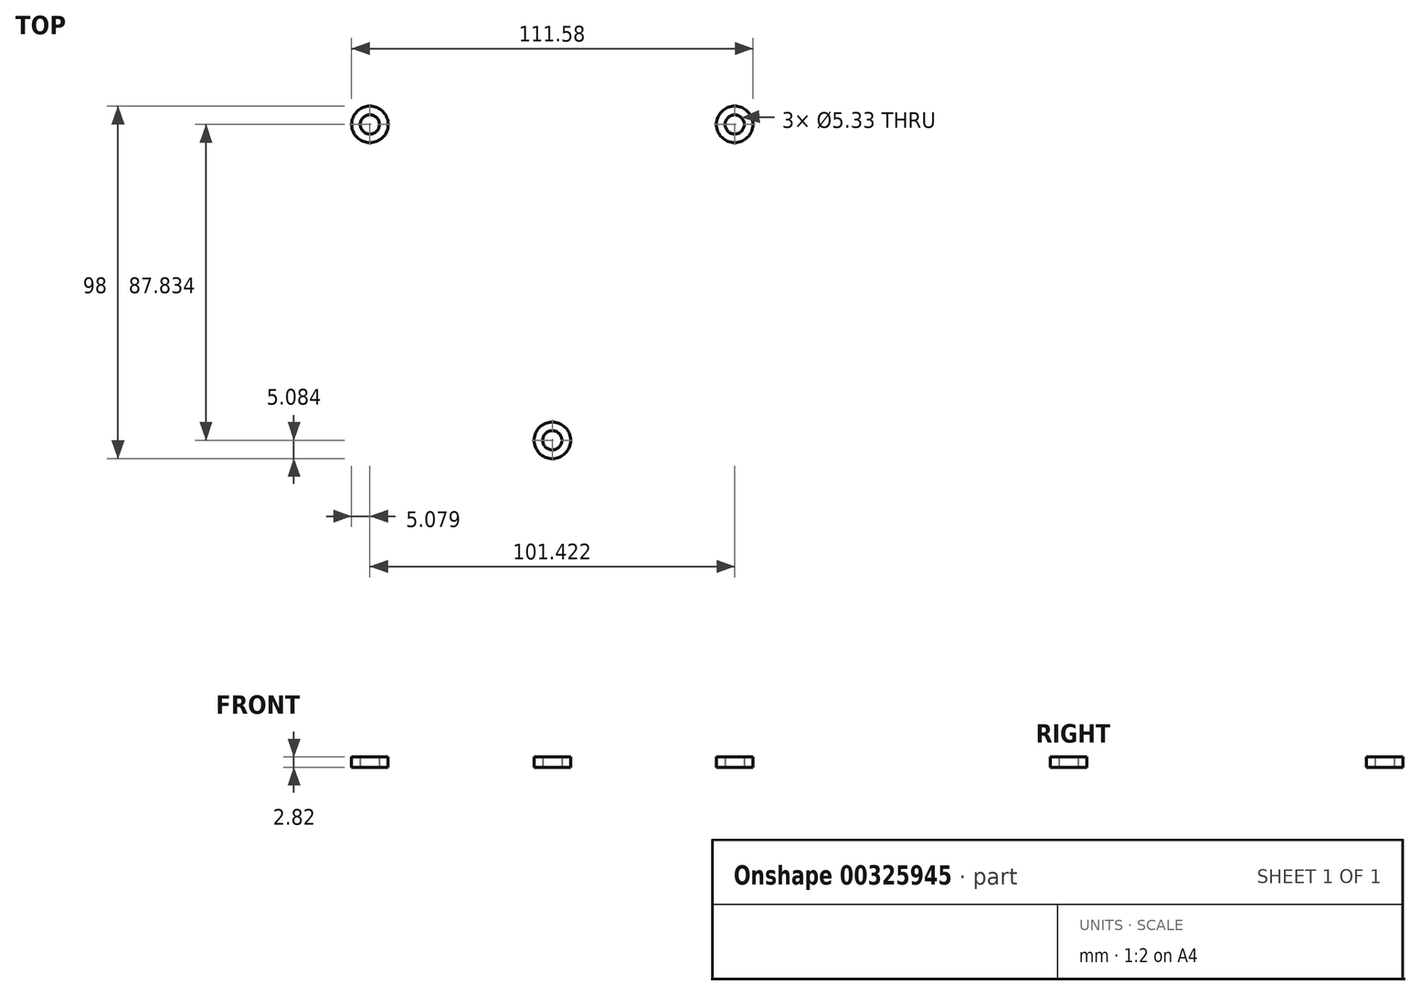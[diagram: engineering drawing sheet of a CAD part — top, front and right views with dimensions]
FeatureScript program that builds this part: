
annotation { "Feature Type Name" : "Feature", "Feature Type Description" : "" }
export const myFeature = defineFeature(function(context is Context, id is Id, definition is map)
    precondition{}
    {
        {
            var Q0;
            Q0=qCreatedBy(makeId("Top.planeOp"),FACE);
            var sketch = newSketch(context, id + "F0", { "sketchPlane" : qUnion([Q0])});
            skCircle(sketch, "E0", {"center": v(0, 0) * mm, "radius": 58.56 * mm});
            skCircle(sketch, "E1", {"center": v(-50.71, 29.28) * mm, "radius": 2.67 * mm});
            skCircle(sketch, "E2", {"center": v(-50.71, 29.28) * mm, "radius": 5.08 * mm});
            skCircle(sketch, "E3", {"center": v(50.71, 29.28) * mm, "radius": 2.67 * mm});
            skCircle(sketch, "E4", {"center": v(50.71, 29.28) * mm, "radius": 5.08 * mm});
            skCircle(sketch, "E5", {"center": v(0, -58.56) * mm, "radius": 2.67 * mm});
            skCircle(sketch, "E6", {"center": v(0, -58.56) * mm, "radius": 5.08 * mm});
            skSolve(sketch);
        }
        {
            var Q0;
            {var subQ0=sQuery(id+"F0.wireOp",EDGE,"E4");var subQ1=sQuery(id+"F0.wireOp",EDGE,"E0");var subQ2=makeQuery(id+"F0.imprint","INTERSECT",VERTEX,{"disambiguationData":[OD(0.0)],"derivedFrom":[subQ1,subQ0]});Q0=makeQuery(id+"F0.imprint","IMPRINT",FACE,{"disambiguationData":[TD([[makeQuery(id+"F0.imprint","IMPRINT",EDGE,{"disambiguationData":[TD([[subQ2,-1.0]])],"derivedFrom":subQ1}),-1.0]])]});}
            var Q1;
            {var subQ0=sQuery(id+"F0.wireOp",EDGE,"E2");var subQ1=sQuery(id+"F0.wireOp",EDGE,"E0");var subQ2=makeQuery(id+"F0.imprint","INTERSECT",VERTEX,{"disambiguationData":[OD(0.0)],"derivedFrom":[subQ1,subQ0]});Q1=makeQuery(id+"F0.imprint","IMPRINT",FACE,{"disambiguationData":[TD([[makeQuery(id+"F0.imprint","IMPRINT",EDGE,{"disambiguationData":[TD([[subQ2,-1.0]])],"derivedFrom":subQ1}),-1.0]])]});}
            var Q2;
            {var subQ0=sQuery(id+"F0.wireOp",EDGE,"E6");var subQ1=sQuery(id+"F0.wireOp",EDGE,"E0");var subQ2=makeQuery(id+"F0.imprint","INTERSECT",VERTEX,{"disambiguationData":[OD(0.0)],"derivedFrom":[subQ1,subQ0]});Q2=makeQuery(id+"F0.imprint","IMPRINT",FACE,{"disambiguationData":[TD([[makeQuery(id+"F0.imprint","IMPRINT",EDGE,{"disambiguationData":[TD([[subQ2,-1.0]])],"derivedFrom":subQ1}),-1.0]])]});}
            var Q3;
            {var subQ0=sQuery(id+"F0.wireOp",EDGE,"E4");var subQ1=sQuery(id+"F0.wireOp",EDGE,"E0");var subQ2=makeQuery(id+"F0.imprint","INTERSECT",VERTEX,{"disambiguationData":[OD(0.0)],"derivedFrom":[subQ1,subQ0]});Q3=makeQuery(id+"F0.imprint","IMPRINT",FACE,{"disambiguationData":[TD([[makeQuery(id+"F0.imprint","IMPRINT",EDGE,{"disambiguationData":[TD([[subQ2,-1.0]])],"derivedFrom":subQ1}),1.0]])]});}
            var Q4;
            {var subQ0=sQuery(id+"F0.wireOp",EDGE,"E2");var subQ1=sQuery(id+"F0.wireOp",EDGE,"E0");var subQ2=makeQuery(id+"F0.imprint","INTERSECT",VERTEX,{"disambiguationData":[OD(0.0)],"derivedFrom":[subQ1,subQ0]});Q4=makeQuery(id+"F0.imprint","IMPRINT",FACE,{"disambiguationData":[TD([[makeQuery(id+"F0.imprint","IMPRINT",EDGE,{"disambiguationData":[TD([[subQ2,-1.0]])],"derivedFrom":subQ1}),1.0]])]});}
            var Q5;
            {var subQ0=sQuery(id+"F0.wireOp",EDGE,"E6");var subQ1=sQuery(id+"F0.wireOp",EDGE,"E0");var subQ2=makeQuery(id+"F0.imprint","INTERSECT",VERTEX,{"disambiguationData":[OD(0.0)],"derivedFrom":[subQ1,subQ0]});Q5=makeQuery(id+"F0.imprint","IMPRINT",FACE,{"disambiguationData":[TD([[makeQuery(id+"F0.imprint","IMPRINT",EDGE,{"disambiguationData":[TD([[subQ2,-1.0]])],"derivedFrom":subQ1}),1.0]])]});}
            extrude(context, id + "F1", {"entities" : qUnion([Q0, Q1, Q2, Q3, Q4, Q5]), "depth" : 2.82 * mm});
        }
        {
            var Q0;
            Q0=qCreatedBy(makeId("Top.planeOp"),FACE);
            var sketch = newSketch(context, id + "F2", { "sketchPlane" : qUnion([Q0])});
            skCircle(sketch, "E7", {"center": v(0, 0) * mm, "radius": 58.56 * mm});
            skCircle(sketch, "E8", {"center": v(-50.71, 29.28) * mm, "radius": 2.67 * mm});
            skCircle(sketch, "E9", {"center": v(50.71, 29.28) * mm, "radius": 2.67 * mm});
            skCircle(sketch, "E10", {"center": v(0, -58.56) * mm, "radius": 2.67 * mm});
            skSolve(sketch);
        }
        {
            var Q0;
            Q0=makeQuery(id+"F1.opExtrude","CAP_FACE",FACE,{"disambiguationData":[OSD([sQuery(id+"F0.wireOp",EDGE,"E1"),sQuery(id+"F0.wireOp",EDGE,"E2")])],"isStart":false});
            var sketch = newSketch(context, id + "F3", { "sketchPlane" : qUnion([Q0])});
            skCircle(sketch, "E11", {"center": v(0, 0) * mm, "radius": 69.85 * mm});
            skCircle(sketch, "E12", {"center": v(-50.71, 29.28) * mm, "radius": 5.08 * mm});
            skCircle(sketch, "E13", {"center": v(50.71, 29.28) * mm, "radius": 5.08 * mm});
            skCircle(sketch, "E14", {"center": v(0, -58.56) * mm, "radius": 5.08 * mm});
            skCircle(sketch, "E15", {"center": v(0, 0) * mm, "radius": 13.97 * mm});
            skLineSegment(sketch, "E16", {"start": v(-22, 49.23) * mm, "end": v(21.94, 49.23) * mm});
            skLineSegment(sketch, "E17", {"start": v(24.51, 42.61) * mm, "end": v(2.58, 22.45) * mm});
            skLineSegment(sketch, "E18", {"start": v(-2.58, 22.44) * mm, "end": v(-24.57, 42.6) * mm});
            skLineSegment(sketch, "E19.1.0", {"start": v(-31.63, -43.66) * mm, "end": v(-53.6, -5.62) * mm});
            skLineSegment(sketch, "E19.1.1", {"start": v(-18.15, -13.45) * mm, "end": v(-24.61, -42.58) * mm});
            skLineSegment(sketch, "E19.1.2", {"start": v(-49.16, -0.08) * mm, "end": v(-20.73, -9) * mm});
            skLineSegment(sketch, "E19.2.0", {"start": v(53.63, -5.56) * mm, "end": v(31.66, -43.6) * mm});
            skLineSegment(sketch, "E19.2.1", {"start": v(20.73, -8.99) * mm, "end": v(49.19, -0.03) * mm});
            skLineSegment(sketch, "E19.2.2", {"start": v(24.65, -42.54) * mm, "end": v(18.15, -13.45) * mm});
            skLineSegment(sketch, "E20", {"start": v(-14.2, 15.54) * mm, "end": v(-21.48, 4.1) * mm});
            skLineSegment(sketch, "E21", {"start": v(-28.74, 1.46) * mm, "end": v(-43.86, 6.2) * mm});
            skLineSegment(sketch, "E22", {"start": v(-15.26, 23.63) * mm, "end": v(-26.63, 34.06) * mm});
            skLineSegment(sketch, "E23", {"start": v(-36.26, 32.82) * mm, "end": v(-47.3, 15.7) * mm});
            skLineSegment(sketch, "E24.1.0", {"start": v(-12.84, -25.03) * mm, "end": v(-16.18, -40.1) * mm});
            skLineSegment(sketch, "E24.1.1", {"start": v(-10.3, -47.81) * mm, "end": v(10.05, -48.8) * mm});
            skLineSegment(sketch, "E24.1.2", {"start": v(13.1, -25.62) * mm, "end": v(16.56, -41.08) * mm});
            skLineSegment(sketch, "E24.1.3", {"start": v(-6.36, -20.06) * mm, "end": v(7.2, -20.66) * mm});
            skLineSegment(sketch, "E24.2.0", {"start": v(28.1, 1.4) * mm, "end": v(42.82, 6.03) * mm});
            skLineSegment(sketch, "E24.2.1", {"start": v(46.56, 15) * mm, "end": v(37.24, 33.11) * mm});
            skLineSegment(sketch, "E24.2.2", {"start": v(15.63, 24.16) * mm, "end": v(27.3, 34.89) * mm});
            skLineSegment(sketch, "E24.2.3", {"start": v(20.55, 4.52) * mm, "end": v(14.3, 16.55) * mm});
            skPoint(sketch, "E25.visualSharp", {"position": v(-32.18, 39.15) * mm});
            skArc(sketch, "E25.filletArc", {"start": v(-26.63, 34.06) * mm, "mid": v(-31.73, 35.68) * mm, "end": v(-36.26, 32.82) * mm});
            skPoint(sketch, "E26.visualSharp", {"position": v(-51.81, 8.7) * mm});
            skArc(sketch, "E26.filletArc", {"start": v(-47.3, 15.7) * mm, "mid": v(-47.93, 10.1) * mm, "end": v(-43.86, 6.2) * mm});
            skPoint(sketch, "E27.visualSharp", {"position": v(-11.33, 20.03) * mm});
            skArc(sketch, "E27.filletArc", {"start": v(-14.2, 15.54) * mm, "mid": v(-13.25, 19.78) * mm, "end": v(-15.26, 23.63) * mm});
            skPoint(sketch, "E28.visualSharp", {"position": v(-24.1, 0) * mm});
            skArc(sketch, "E28.filletArc", {"start": v(-28.74, 1.46) * mm, "mid": v(-24.66, 1.55) * mm, "end": v(-21.48, 4.1) * mm});
            skPoint(sketch, "E29.visualSharp", {"position": v(31.71, 49.23) * mm});
            skArc(sketch, "E29.filletArc", {"start": v(24.51, 42.61) * mm, "mid": v(25.49, 46.8) * mm, "end": v(21.94, 49.23) * mm});
            skPoint(sketch, "E30.visualSharp", {"position": v(-31.79, 49.23) * mm});
            skArc(sketch, "E30.filletArc", {"start": v(-22, 49.23) * mm, "mid": v(-25.55, 46.8) * mm, "end": v(-24.57, 42.6) * mm});
            skPoint(sketch, "E31.visualSharp", {"position": v(0, 20.08) * mm});
            skArc(sketch, "E31.filletArc", {"start": v(-2.58, 22.44) * mm, "mid": v(0, 21.44) * mm, "end": v(2.58, 22.45) * mm});
            skPoint(sketch, "E32.visualSharp", {"position": v(33.43, 40.52) * mm});
            skArc(sketch, "E32.filletArc", {"start": v(37.24, 33.11) * mm, "mid": v(32.7, 36.46) * mm, "end": v(27.3, 34.89) * mm});
            skPoint(sketch, "E33.visualSharp", {"position": v(50, 8.3) * mm});
            skArc(sketch, "E33.filletArc", {"start": v(42.82, 6.03) * mm, "mid": v(46.77, 9.64) * mm, "end": v(46.56, 15) * mm});
            skPoint(sketch, "E34.visualSharp", {"position": v(23.01, -0.2) * mm});
            skArc(sketch, "E34.filletArc", {"start": v(20.55, 4.52) * mm, "mid": v(23.75, 1.59) * mm, "end": v(28.1, 1.4) * mm});
            skPoint(sketch, "E35.visualSharp", {"position": v(12.05, 20.87) * mm});
            skArc(sketch, "E35.filletArc", {"start": v(15.63, 24.16) * mm, "mid": v(13.67, 20.58) * mm, "end": v(14.3, 16.55) * mm});
            skPoint(sketch, "E36.visualSharp", {"position": v(12.05, -20.87) * mm});
            skArc(sketch, "E36.filletArc", {"start": v(13.1, -25.62) * mm, "mid": v(10.99, -22.13) * mm, "end": v(7.2, -20.66) * mm});
            skPoint(sketch, "E37.visualSharp", {"position": v(-11.68, -19.83) * mm});
            skArc(sketch, "E37.filletArc", {"start": v(-6.36, -20.06) * mm, "mid": v(-10.5, -21.37) * mm, "end": v(-12.84, -25.03) * mm});
            skPoint(sketch, "E38.visualSharp", {"position": v(-17.82, -47.45) * mm});
            skArc(sketch, "E38.filletArc", {"start": v(-16.18, -40.1) * mm, "mid": v(-15.03, -45.32) * mm, "end": v(-10.3, -47.81) * mm});
            skPoint(sketch, "E39.visualSharp", {"position": v(18.38, -49.22) * mm});
            skArc(sketch, "E39.filletArc", {"start": v(10.05, -48.8) * mm, "mid": v(15.22, -46.56) * mm, "end": v(16.56, -41.08) * mm});
            skPoint(sketch, "E40.visualSharp", {"position": v(17.4, -10.04) * mm});
            skArc(sketch, "E40.filletArc", {"start": v(20.73, -8.99) * mm, "mid": v(18.57, -10.72) * mm, "end": v(18.15, -13.45) * mm});
            skPoint(sketch, "E41.visualSharp", {"position": v(58.53, 2.92) * mm});
            skArc(sketch, "E41.filletArc", {"start": v(53.63, -5.56) * mm, "mid": v(53.3, -1.27) * mm, "end": v(49.19, -0.03) * mm});
            skPoint(sketch, "E42.visualSharp", {"position": v(26.78, -52.08) * mm});
            skArc(sketch, "E42.filletArc", {"start": v(24.65, -42.54) * mm, "mid": v(27.79, -45.47) * mm, "end": v(31.66, -43.6) * mm});
            skPoint(sketch, "E43.visualSharp", {"position": v(-58.49, 2.85) * mm});
            skArc(sketch, "E43.filletArc", {"start": v(-49.16, -0.08) * mm, "mid": v(-53.27, -1.33) * mm, "end": v(-53.6, -5.62) * mm});
            skPoint(sketch, "E44.visualSharp", {"position": v(-17.4, -10.04) * mm});
            skArc(sketch, "E44.filletArc", {"start": v(-18.15, -13.45) * mm, "mid": v(-18.57, -10.72) * mm, "end": v(-20.73, -9) * mm});
            skPoint(sketch, "E45.visualSharp", {"position": v(-26.74, -52.14) * mm});
            skArc(sketch, "E45.filletArc", {"start": v(-31.63, -43.66) * mm, "mid": v(-27.75, -45.52) * mm, "end": v(-24.61, -42.58) * mm});
            skSolve(sketch);
        }
        {
            var Q0;
            Q0 = qSketchRegion(id + "F3", true);
            extrude(context, id + "F4", {"entities" : qUnion([Q0]), "oppositeDirection" : true, "depth" : 3.8 * mm});
        }
        {
            var Q0;
            Q0=qCreatedBy(makeId("Front.planeOp"),FACE);
            var sketch = newSketch(context, id + "F5", { "sketchPlane" : qUnion([Q0])});
            skLineSegment(sketch, "E46", {"start": v(0, 0) * mm, "end": v(0, 28.45) * mm});
            skLineSegment(sketch, "E47", {"start": v(76.2, 28.45) * mm, "end": v(77.98, 28.45) * mm});
            skFitSpline(sketch, "E48", {"points": [v(69.65, -0.95) * mm, v(79.86, 4.92) * mm, v(81.52, 11.34) * mm, v(82.3, 20.58) * mm, v(82.3, 28.45) * mm], "startDerivative": vector(67.84, 9.88) * mm, "endDerivative": vector(2.95, 34.79) * mm});
            skFitSpline(sketch, "E49", {"points": [v(69.62, 2.82) * mm, v(74.37, 5.44) * mm, v(77.04, 10.96) * mm, v(76.2, 20.61) * mm, v(76.2, 28.45) * mm], "startDerivative": vector(17.5, 1.5) * mm, "endDerivative": vector(-2.21, 24.56) * mm});
            skLineSegment(sketch, "E50", {"start": v(69.65, -0.95) * mm, "end": v(69.62, 2.82) * mm});
            skLineSegment(sketch, "E51", {"start": v(77.98, 28.45) * mm, "end": v(77.98, 22.1) * mm});
            skLineSegment(sketch, "E52", {"start": v(77.98, 22.1) * mm, "end": v(79.76, 22.1) * mm});
            skLineSegment(sketch, "E53", {"start": v(79.76, 22.1) * mm, "end": v(79.76, 28.45) * mm});
            skLineSegment(sketch, "E54.trimOffspring", {"start": v(79.76, 28.45) * mm, "end": v(82.3, 28.45) * mm});
            skSolve(sketch);
        }
        {
            var Q0;
            Q0=makeQuery(id+"F5.imprint","IMPRINT",FACE,{"disambiguationData":[TD([[makeQuery(id+"F5.imprint","IMPRINT",EDGE,{"derivedFrom":sQuery(id+"F5.wireOp",EDGE,"E47")}),-1.0]])]});
            var Q1;
            Q1=sQuery(id+"F5.wireOp",EDGE,"E46");
            revolve(context, id + "F6", {"operationType" : NewBodyOperationType.ADD, "entities" : qUnion([Q0]), "axis" : qUnion([Q1]), "revolveType" : RevolveType.FULL});
        }
        {
            var Q0;
            Q0=makeQuery(id+"F6.opRevolve","SWEPT_FACE",FACE,{"disambiguationData":[OSD([sQuery(id+"F5.wireOp",EDGE,"E54.trimOffspring")])]});
            var sketch = newSketch(context, id + "F7", { "sketchPlane" : qUnion([Q0])});
            skLineSegment(sketch, "E55", {"start": v(0, 0) * mm, "end": v(-37.78, 76.54) * mm});
            skLineSegment(sketch, "E56.0", {"start": v(-5.01, -2.47) * mm, "end": v(-42.8, 74.06) * mm});
            skCircle(sketch, "E57.0", {"center": v(0, 0) * mm, "radius": 75.95 * mm});
            skLineSegment(sketch, "E58.0", {"start": v(5.01, 2.47) * mm, "end": v(-32.77, 79.01) * mm});
            skLineSegment(sketch, "E59", {"start": v(-37.75, 63.85) * mm, "end": v(-27.73, 68.8) * mm});
            skLineSegment(sketch, "E60", {"start": v(-42.8, 74.06) * mm, "end": v(-32.77, 79.01) * mm});
            skSolve(sketch);
        }
        {
            var Q0;
            Q0 = qSketchRegion(id + "F7", true);
            extrude(context, id + "F8", {"entities" : qUnion([Q0]), "operationType" : NewBodyOperationType.REMOVE, "oppositeDirection" : true, "depth" : 12.7 * mm});
        }
        {
            var Q0;
            Q0=makeQuery(id+"F8.boolean.opBoolean","COPY",EDGE,{"derivedFrom":makeQuery(id+"F8.opExtrude","CAP_EDGE",EDGE,{"disambiguationData":[OSD([sQuery(id+"F7.wireOp",EDGE,"E58.0")])],"isStart":false})});
            var Q1;
            Q1=makeQuery(id+"F8.boolean.opBoolean","COPY",EDGE,{"derivedFrom":makeQuery(id+"F8.opExtrude","CAP_EDGE",EDGE,{"disambiguationData":[OSD([sQuery(id+"F7.wireOp",EDGE,"E56.0")])],"isStart":false})});
            fillet(context, id + "F9", {"entities" : qUnion([Q0, Q1]), "radius" : 5.08 * mm, "tangentPropagation" : true, "allowEdgeOverflow" : false});
        }
    });
